# Revit family: PV_Compact_PN25_DN125_(90-350kPa)_RFA_2018
name_source: partatom
category: Pipe Accessories
revit_build: Autodesk Revit LT 2018 (Build: 20180329_1100(x64)
units: mm (PartAtom-declared; Revit-internal decimal feet)

## family parameters
Always vertical = Yes
Cut with Voids When Loaded = No
Part Type = Valve - Breaks Into
Round Connector Dimension = Use Diameter
Shared = No
Work Plane-Based = No

## types (3) — shared parameters
CAT0 = Yes
Description = Nastavitelný regulátor diferenčního tlaku
L2D = 400 mm
L2D_Min = 30 mm  [stored 0.0984252 ft]
MC Pressure Drop Maximum Value = 0.0 Pa
MC Pressure Drop Minimum Value = 0.0 Pa
MC Use Limits From Balancing Method = No
Manufacturer = Hydronic Systems Prague s.r.o.
QmdConnectorList = 301;D;302;D
URL = www.hydronic.cz
W2D = 125 mm  [stored 0.410105 ft]
magiPartTypeId = 304
magiProductFamilyId = 9e0837c0ac1a48c1a74a343bd519c1
zero-valued in all types: MC Throttling Maximum Value, MC Throttling Minimum Value

## per-type parameters (varying)
| type | D | DF2 | H1 | H2 | H3 | H4 | H6 | L2 | L3 | L4 | LF | LF2 | LF__ve | MC Product Code | R1 | R3 | R4 | Type Comments | magiProductId |
| PV Compact PN25 DN125 (90-350kPa) | 125 mm | 135 mm  [stored 0.442913 ft] | 203 mm | 101 mm | 34 mm | 41 mm  [stored 0.134514 ft] | 226 mm | 200 mm  [stored 0.656168 ft] | 336 mm  [stored 1.10236 ft] | 188 mm  [stored 0.616798 ft] | 32 mm  [stored 0.104987 ft] | 16 mm  [stored 0.0524934 ft] | -32 mm  [stored -0.104987 ft] | 53-3333 DN125 PN25; nastavitelný rozsah dp=20~100kPa; Q=40,3~161 m3/h;  kvs=170 | 100 mm  [stored 0.328084 ft] | 70 mm  [stored 0.229659 ft] | 70 mm  [stored 0.229659 ft] | PŘÍRUBOVÝ; PN25; dpmax=1000kPa; -10~+120°C | 828af78972b74e11b5ab1c4abc9b81 |
| PV Compact PN25 DN150 (90-350kPa) | 150 mm | 143 mm | 214 mm | 107 mm | 36 mm | 43 mm | 256 mm | 240 mm  [stored 0.787402 ft] | 403 mm | 226 mm | 38 mm | 19 mm | -38 mm | 53-3336 DN150 PN25; nastavitelný rozsah dp=20~100kPa; Q=59,3~123 m3/h;  kvs=250 | 120 mm  [stored 0.393701 ft] | 74 mm | 84 mm  [stored 0.275591 ft] | PŘÍRUBOVÝ; PN25; dpmax=1000kPa; -10~+110°C | 3c848b5675884766961bbc36692fc4 |
| PV Compact PN25 DN200 (90-350kPa) | 200 mm | 190 mm  [stored 0.62336 ft] | 285 mm  [stored 0.935039 ft] | 143 mm | 48 mm  [stored 0.15748 ft] | 57 mm | 150 mm  [stored 0.492126 ft] | 300 mm  [stored 0.984252 ft] | 504 mm | 282 mm  [stored 0.925197 ft] | 48 mm  [stored 0.15748 ft] | 24 mm  [stored 0.0787402 ft] | -48 mm  [stored -0.15748 ft] | 53-3339 DN200 PN25; nastavitelný rozsah dp=20~100kPa; Q=65,2~261 m3/h;  kvs=275 | 150 mm  [stored 0.492126 ft] | 99 mm | 105 mm  [stored 0.344488 ft] | PŘÍRUBOVÝ; PN25; dpmax=1000kPa; -10~+110°C | 91c75d4260f940c99372a7e9d4703c |

note: [stored X ft] marks values corroborated as IEEE doubles in the binary element streams (Revit-internal decimal feet)

## geometry (parser evidence)
native form markers: Sweep x1
no freeform markers — native parametric forms only
